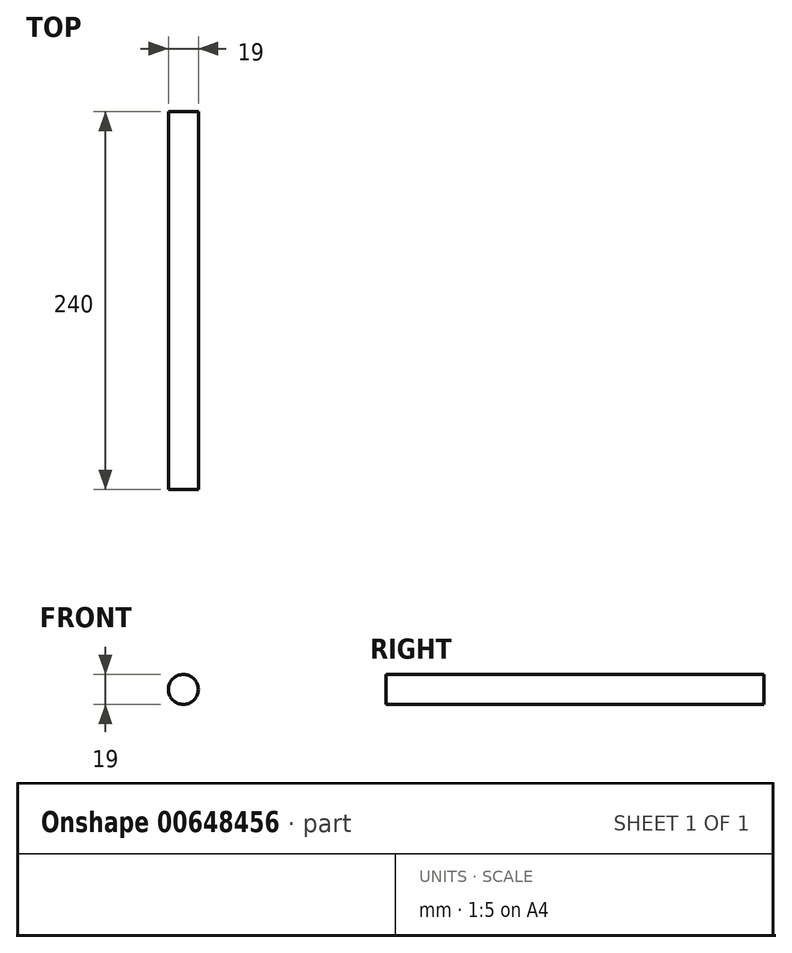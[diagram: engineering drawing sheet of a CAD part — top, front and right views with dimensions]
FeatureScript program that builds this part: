
annotation { "Feature Type Name" : "Feature", "Feature Type Description" : "" }
export const myFeature = defineFeature(function(context is Context, id is Id, definition is map)
    precondition{}
    {
        {
            var Q0;
            Q0=qCreatedBy(makeId("Front.planeOp"),FACE);
            var sketch = newSketch(context, id + "F0", { "sketchPlane" : qUnion([Q0])});
            skCircle(sketch, "E0", {"center": v(0, 0) * mm, "radius": 9.5 * mm});
            skSolve(sketch);
        }
        {
            var Q0;
            Q0 = qSketchRegion(id + "F0", true);
            extrude(context, id + "F1", {"entities" : qUnion([Q0]), "oppositeDirection" : true, "depth" : 240 * mm, "offsetDistance" : 25 * mm});
        }
    });
